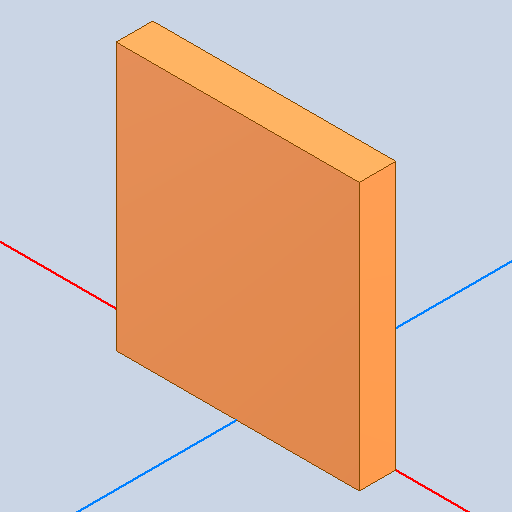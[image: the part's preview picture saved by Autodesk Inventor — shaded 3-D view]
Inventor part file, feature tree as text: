
AUTODESK INVENTOR PART (.ipt)
format: ipt  version: 2022 (Build 260153000, 153)  size: 92,160 bytes
history: native  units: mm
features: other x2, extrude x1
ambient origin geometry x8: Origin, YZ Plane, XZ Plane, XY Plane, X Axis, Y Axis, Z Axis, Center Point
bodies: Body1 (feature_tree)
feature tree (3):
  other  "Твердое тело1"
  extrude  "Выдавливание1"  Depth=1.0mm TaperAngle=0.0deg
  other  "SOT223, U2_SOT223_14"
